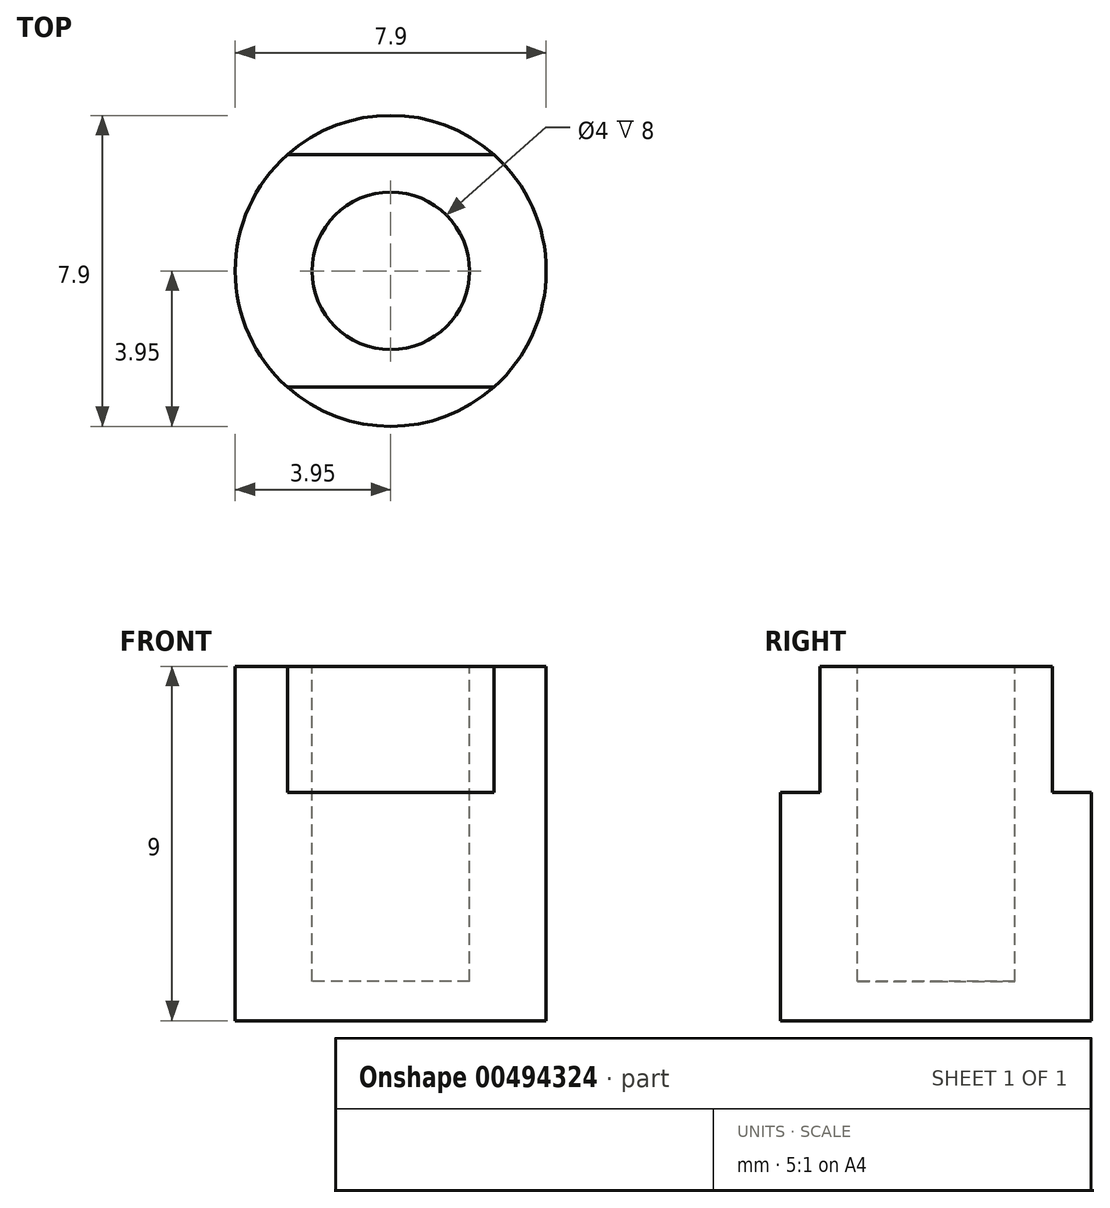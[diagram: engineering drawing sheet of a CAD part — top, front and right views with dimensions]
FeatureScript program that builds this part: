
annotation { "Feature Type Name" : "Feature", "Feature Type Description" : "" }
export const myFeature = defineFeature(function(context is Context, id is Id, definition is map)
    precondition{}
    {
        {
            var Q0;
            Q0=qCreatedBy(makeId("Top.planeOp"),FACE);
            var sketch = newSketch(context, id + "F0", { "sketchPlane" : qUnion([Q0])});
            skCircle(sketch, "E0", {"center": v(0, 0) * mm, "radius": 3.95 * mm});
            skSolve(sketch);
        }
        {
            var Q0;
            Q0=makeQuery(id+"F0.imprint","IMPRINT",FACE,{"disambiguationData":[TD([[makeQuery(id+"F0.imprint","IMPRINT",EDGE,{"derivedFrom":sQuery(id+"F0.wireOp",EDGE,"E0")}),1.0]])]});
            extrude(context, id + "F1", {"entities" : qUnion([Q0]), "depth" : 9 * mm});
        }
        {
            var Q0;
            Q0=makeQuery(id+"F1.opExtrude","CAP_FACE",FACE,{"disambiguationData":[OSD([sQuery(id+"F0.wireOp",EDGE,"E0")])],"isStart":false});
            var sketch = newSketch(context, id + "F2", { "sketchPlane" : qUnion([Q0])});
            skLineSegment(sketch, "E1.bottom", {"start": v(-2.63, 2.95) * mm, "end": v(2.63, 2.95) * mm});
            skLineSegment(sketch, "E1.top", {"start": v(-2.63, -2.95) * mm, "end": v(2.63, -2.95) * mm});
            skPoint(sketch, "E1.middle", {"position": v(0, 0) * mm});
            skSolve(sketch);
        }
        {
            var Q0;
            {var subQ0=sQuery(id+"F2.wireOp",EDGE,"E1.top");Q0=makeQuery(id+"F2.imprint","IMPRINT",FACE,{"disambiguationData":[TD([[makeQuery(id+"F2.imprint","IMPRINT",EDGE,{"derivedFrom":subQ0}),-1.0]])]});}
            var Q1;
            {var subQ0=sQuery(id+"F2.wireOp",EDGE,"E1.bottom");Q1=makeQuery(id+"F2.imprint","IMPRINT",FACE,{"disambiguationData":[TD([[makeQuery(id+"F2.imprint","IMPRINT",EDGE,{"derivedFrom":subQ0}),1.0]])]});}
            extrude(context, id + "F3", {"entities" : qUnion([Q0, Q1]), "operationType" : NewBodyOperationType.REMOVE, "oppositeDirection" : true, "depth" : 3.2 * mm});
        }
        {
            var Q0;
            Q0=makeQuery(id+"F1.opExtrude","CAP_FACE",FACE,{"disambiguationData":[OSD([sQuery(id+"F0.wireOp",EDGE,"E0")])],"isStart":false});
            var sketch = newSketch(context, id + "F4", { "sketchPlane" : qUnion([Q0])});
            skCircle(sketch, "E2", {"center": v(0, 0) * mm, "radius": 2 * mm});
            skSolve(sketch);
        }
        {
            var Q0;
            Q0=makeQuery(id+"F4.imprint","IMPRINT",FACE,{"disambiguationData":[TD([[makeQuery(id+"F4.imprint","IMPRINT",EDGE,{"derivedFrom":sQuery(id+"F4.wireOp",EDGE,"E2")}),1.0]])]});
            extrude(context, id + "F5", {"entities" : qUnion([Q0]), "operationType" : NewBodyOperationType.REMOVE, "oppositeDirection" : true, "depth" : 8 * mm});
        }
    });
